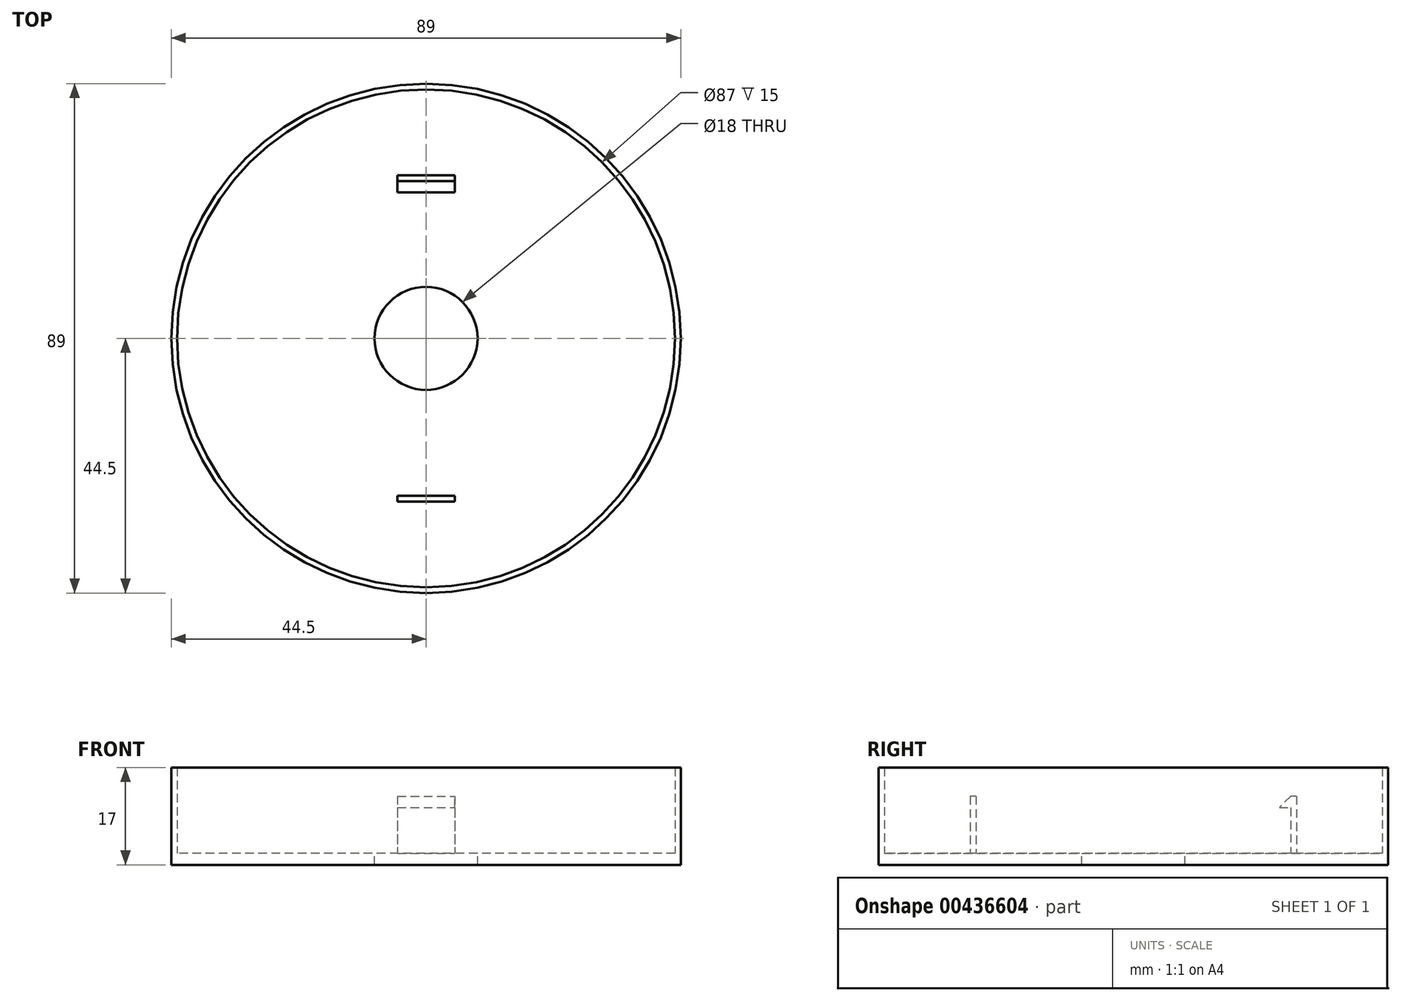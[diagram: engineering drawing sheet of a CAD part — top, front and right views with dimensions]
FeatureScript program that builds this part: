
annotation { "Feature Type Name" : "Feature", "Feature Type Description" : "" }
export const myFeature = defineFeature(function(context is Context, id is Id, definition is map)
    precondition{}
    {
        {
            var Q0;
            Q0=qCreatedBy(makeId("Top.planeOp"),FACE);
            var sketch = newSketch(context, id + "F0", { "sketchPlane" : qUnion([Q0])});
            skCircle(sketch, "E0", {"center": v(0, 0) * mm, "radius": 44.5 * mm});
            skSolve(sketch);
        }
        {
            var Q0;
            Q0 = qSketchRegion(id + "F0", true);
            var Q1;
            Q1 = qConstructionFilter(qBodyType(qCreatedBy(id + "F0" ,EDGE), BodyType.WIRE), ConstructionObject.NO);
            extrude(context, id + "F1", {"entities" : qUnion([Q0]), "surfaceEntities" : qUnion([Q1]), "depth" : 2 * mm});
        }
        {
            var Q0;
            Q0=makeQuery(id+"F1.opExtrude","CAP_FACE",FACE,{"disambiguationData":[OSD([sQuery(id+"F0.wireOp",EDGE,"E0")])],"isStart":false});
            var sketch = newSketch(context, id + "F2", { "sketchPlane" : qUnion([Q0])});
            skCircle(sketch, "E1", {"center": v(0, 0) * mm, "radius": 43.5 * mm});
            skCircle(sketch, "E2", {"center": v(0, 0) * mm, "radius": 44.5 * mm});
            skSolve(sketch);
        }
        {
            var Q0;
            Q0 = qSketchRegion(id + "F2", true);
            extrude(context, id + "F3", {"entities" : qUnion([Q0]), "operationType" : NewBodyOperationType.ADD, "depth" : 15 * mm});
        }
        {
            var Q0;
            Q0=makeQuery(id+"F1.opExtrude","CAP_FACE",FACE,{"disambiguationData":[OSD([sQuery(id+"F0.wireOp",EDGE,"E0")])],"isStart":false});
            var sketch = newSketch(context, id + "F4", { "sketchPlane" : qUnion([Q0])});
            skCircle(sketch, "E3", {"center": v(0, 0) * mm, "radius": 9 * mm});
            skSolve(sketch);
        }
        {
            var Q0;
            Q0 = qSketchRegion(id + "F4", true);
            extrude(context, id + "F5", {"entities" : qUnion([Q0]), "operationType" : NewBodyOperationType.REMOVE, "oppositeDirection" : true, "depth" : 25 * mm});
        }
        {
            assignVariable(context, id + "F6", {"name" : "sensor_clip_height", "anyValue" : 10});
        }
        {
            var Q0;
            Q0=makeQuery(id+"F1.opExtrude","CAP_FACE",FACE,{"disambiguationData":[OSD([sQuery(id+"F0.wireOp",EDGE,"E0")])],"isStart":false});
            var sketch = newSketch(context, id + "F7", { "sketchPlane" : qUnion([Q0])});
            skLineSegment(sketch, "E4.bottom", {"start": v(-5, 28.5) * mm, "end": v(5, 28.5) * mm});
            skLineSegment(sketch, "E4.top", {"start": v(-5, 27.5) * mm, "end": v(5, 27.5) * mm});
            skLineSegment(sketch, "E4.left", {"start": v(-5, 28.5) * mm, "end": v(-5, 27.5) * mm});
            skLineSegment(sketch, "E4.right", {"start": v(5, 28.5) * mm, "end": v(5, 27.5) * mm});
            skLineSegment(sketch, "E5.bottom", {"start": v(-5, -27.5) * mm, "end": v(5, -27.5) * mm});
            skLineSegment(sketch, "E5.top", {"start": v(-5, -28.5) * mm, "end": v(5, -28.5) * mm});
            skLineSegment(sketch, "E5.left", {"start": v(-5, -27.5) * mm, "end": v(-5, -28.5) * mm});
            skLineSegment(sketch, "E5.right", {"start": v(5, -27.5) * mm, "end": v(5, -28.5) * mm});
            skSolve(sketch);
        }
        {
            var Q0;
            Q0 = qSketchRegion(id + "F7", true);
            extrude(context, id + "F8", {"entities" : qUnion([Q0]), "operationType" : NewBodyOperationType.ADD, "depth" : (getVariable(context, 'sensor_clip_height')) * mm});
        }
        {
            assignVariable(context, id + "F9", {"name" : "sensor_clip_hook", "anyValue" : 2});
        }
        {
            var Q0;
            Q0=makeQuery(id+"F8.opExtrude","SWEPT_FACE",FACE,{"disambiguationData":[OSD([sQuery(id+"F7.wireOp",EDGE,"E4.top")])]});
            var sketch = newSketch(context, id + "F10", { "sketchPlane" : qUnion([Q0])});
            skLineSegment(sketch, "E6.bottom", {"start": v(-5, 12) * mm, "end": v(5, 12) * mm});
            skLineSegment(sketch, "E6.top", {"start": v(-5, 10) * mm, "end": v(5, 10) * mm});
            skLineSegment(sketch, "E6.left", {"start": v(-5, 12) * mm, "end": v(-5, 10) * mm});
            skLineSegment(sketch, "E6.right", {"start": v(5, 12) * mm, "end": v(5, 10) * mm});
            skSolve(sketch);
        }
        {
            var Q0;
            Q0 = qSketchRegion(id + "F10", true);
            extrude(context, id + "F11", {"entities" : qUnion([Q0]), "operationType" : NewBodyOperationType.ADD, "depth" : (getVariable(context, 'sensor_clip_hook')) * mm});
        }
        {
            var Q0;
            Q0=makeQuery(id+"F11.opExtrude","CAP_EDGE",EDGE,{"disambiguationData":[OSD([sQuery(id+"F10.wireOp",EDGE,"E6.bottom")])],"isStart":false});
            chamfer(context, id + "F12", {"entities" : qUnion([Q0]), "width" : 2 * mm, "tangentPropagation" : true});
        }
    });
